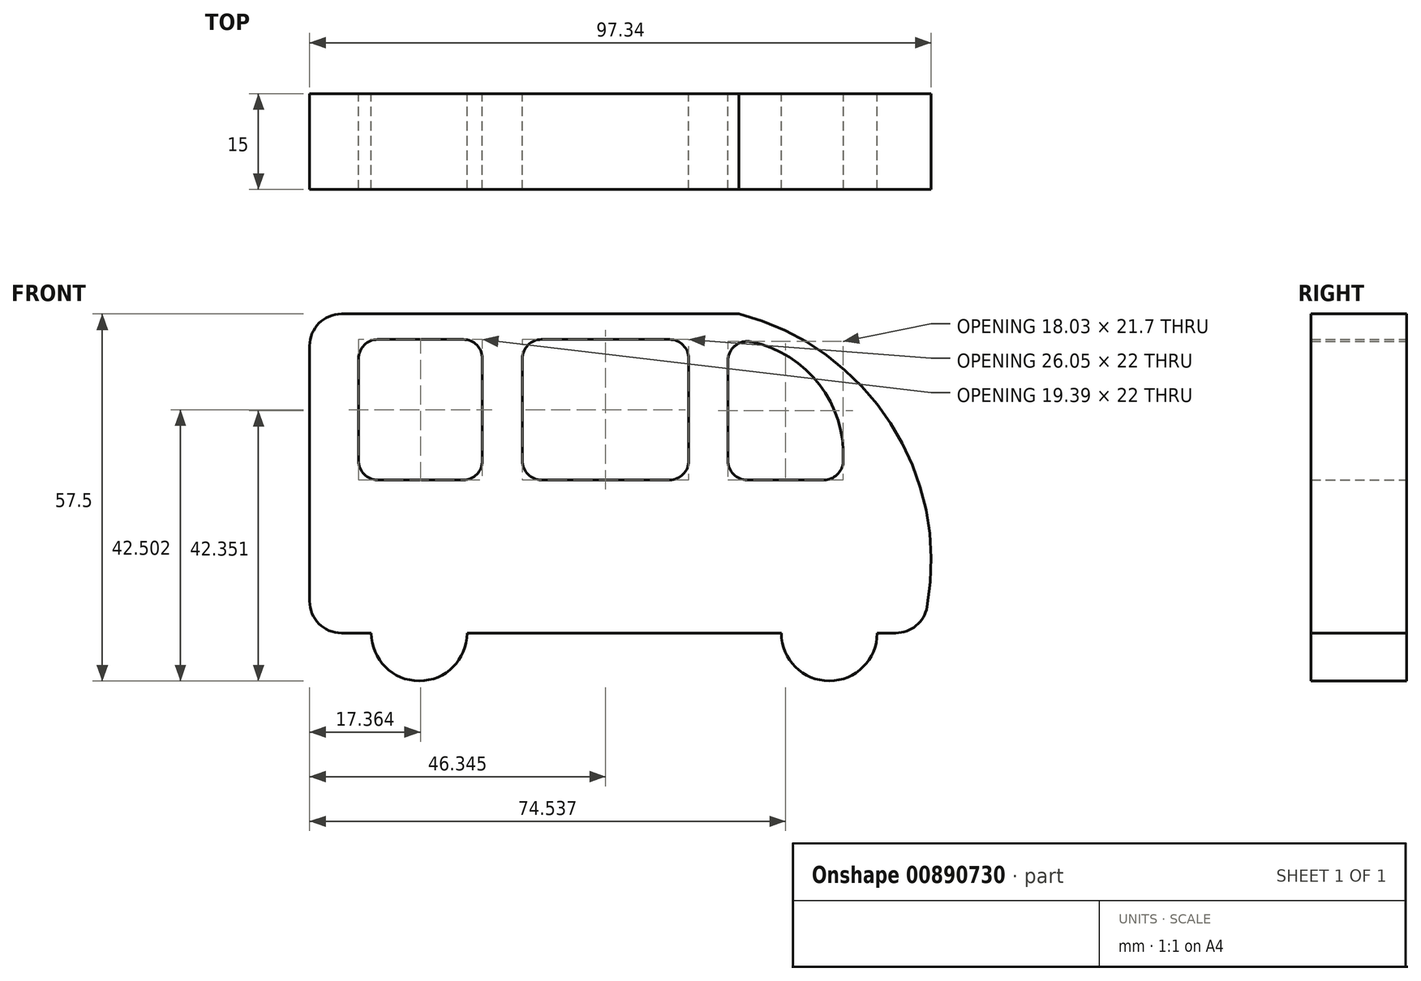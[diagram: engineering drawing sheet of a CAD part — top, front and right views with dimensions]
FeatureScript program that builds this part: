
annotation { "Feature Type Name" : "Feature", "Feature Type Description" : "" }
export const myFeature = defineFeature(function(context is Context, id is Id, definition is map)
    precondition{}
    {
        {
            var Q0;
            Q0=qCreatedBy(makeId("Front.planeOp"),FACE);
            var sketch = newSketch(context, id + "F0", { "sketchPlane" : qUnion([Q0])});
            skLineSegment(sketch, "E0.bottom", {"start": v(-16.93, 66.61) * mm, "end": v(45.28, 66.61) * mm});
            skLineSegment(sketch, "E0.top", {"start": v(-16.93, 16.61) * mm, "end": v(-12.27, 16.61) * mm});
            skLineSegment(sketch, "E0.left", {"start": v(-21.93, 61.61) * mm, "end": v(-21.93, 21.61) * mm});
            skArc(sketch, "E1", {"start": v(-12.27, 16.61) * mm, "mid": v(-4.77, 9.11) * mm, "end": v(2.73, 16.61) * mm});
            skArc(sketch, "E2", {"start": v(51.95, 16.61) * mm, "mid": v(59.45, 9.11) * mm, "end": v(66.95, 16.61) * mm});
            skArc(sketch, "E3", {"start": v(74.77, 20.72) * mm, "mid": v(69.06, 49.47) * mm, "end": v(45.28, 66.61) * mm});
            skPoint(sketch, "E4.visualSharp", {"position": v(-21.93, 66.61) * mm});
            skArc(sketch, "E4.filletArc", {"start": v(-16.93, 66.61) * mm, "mid": v(-20.47, 65.15) * mm, "end": v(-21.93, 61.61) * mm});
            skPoint(sketch, "E5.visualSharp", {"position": v(-21.93, 16.61) * mm});
            skArc(sketch, "E5.filletArc", {"start": v(-21.93, 21.61) * mm, "mid": v(-20.47, 18.08) * mm, "end": v(-16.93, 16.61) * mm});
            skPoint(sketch, "E6.visualSharp", {"position": v(73.8, 16.61) * mm});
            skArc(sketch, "E6.filletArc", {"start": v(69.85, 16.61) * mm, "mid": v(73.06, 17.77) * mm, "end": v(74.77, 20.72) * mm});
            skLineSegment(sketch, "E7.trimOffspring", {"start": v(2.73, 16.61) * mm, "end": v(51.95, 16.61) * mm});
            skLineSegment(sketch, "E8.trimOffspring", {"start": v(66.95, 16.61) * mm, "end": v(69.85, 16.61) * mm});
            skLineSegment(sketch, "E9", {"start": v(58.63, 40.61) * mm, "end": v(46.6, 40.61) * mm});
            skLineSegment(sketch, "E10", {"start": v(43.6, 43.61) * mm, "end": v(43.6, 59.31) * mm});
            skLineSegment(sketch, "E11.bottom", {"start": v(-11.26, 62.61) * mm, "end": v(2.13, 62.61) * mm});
            skLineSegment(sketch, "E11.top", {"start": v(-11.26, 40.61) * mm, "end": v(2.13, 40.61) * mm});
            skLineSegment(sketch, "E11.left", {"start": v(-14.26, 59.61) * mm, "end": v(-14.26, 43.61) * mm});
            skLineSegment(sketch, "E11.right", {"start": v(5.13, 59.61) * mm, "end": v(5.13, 43.61) * mm});
            skLineSegment(sketch, "E12.bottom", {"start": v(14.39, 62.61) * mm, "end": v(34.44, 62.61) * mm});
            skLineSegment(sketch, "E12.top", {"start": v(14.39, 40.61) * mm, "end": v(34.44, 40.61) * mm});
            skLineSegment(sketch, "E12.left", {"start": v(11.39, 59.61) * mm, "end": v(11.39, 43.61) * mm});
            skLineSegment(sketch, "E12.right", {"start": v(37.44, 59.61) * mm, "end": v(37.44, 43.61) * mm});
            skArc(sketch, "E13", {"start": v(61.62, 43.43) * mm, "mid": v(57.93, 55.54) * mm, "end": v(47.2, 62.25) * mm});
            skPoint(sketch, "E14.visualSharp", {"position": v(-14.26, 40.61) * mm});
            skArc(sketch, "E14.filletArc", {"start": v(-14.26, 43.61) * mm, "mid": v(-13.38, 41.5) * mm, "end": v(-11.26, 40.61) * mm});
            skPoint(sketch, "E15.visualSharp", {"position": v(-14.26, 62.61) * mm});
            skArc(sketch, "E15.filletArc", {"start": v(-11.26, 62.61) * mm, "mid": v(-13.38, 61.73) * mm, "end": v(-14.26, 59.61) * mm});
            skPoint(sketch, "E16.visualSharp", {"position": v(5.13, 62.61) * mm});
            skArc(sketch, "E16.filletArc", {"start": v(5.13, 59.61) * mm, "mid": v(4.25, 61.73) * mm, "end": v(2.13, 62.61) * mm});
            skPoint(sketch, "E17.visualSharp", {"position": v(5.13, 40.61) * mm});
            skArc(sketch, "E17.filletArc", {"start": v(2.13, 40.61) * mm, "mid": v(4.25, 41.5) * mm, "end": v(5.13, 43.61) * mm});
            skPoint(sketch, "E18.visualSharp", {"position": v(11.39, 40.61) * mm});
            skArc(sketch, "E18.filletArc", {"start": v(11.39, 43.61) * mm, "mid": v(12.27, 41.5) * mm, "end": v(14.39, 40.61) * mm});
            skPoint(sketch, "E19.visualSharp", {"position": v(11.39, 62.61) * mm});
            skArc(sketch, "E19.filletArc", {"start": v(14.39, 62.61) * mm, "mid": v(12.27, 61.73) * mm, "end": v(11.39, 59.61) * mm});
            skPoint(sketch, "E20.visualSharp", {"position": v(37.44, 62.61) * mm});
            skArc(sketch, "E20.filletArc", {"start": v(37.44, 59.61) * mm, "mid": v(36.56, 61.73) * mm, "end": v(34.44, 62.61) * mm});
            skPoint(sketch, "E21.visualSharp", {"position": v(37.44, 40.61) * mm});
            skArc(sketch, "E21.filletArc", {"start": v(34.44, 40.61) * mm, "mid": v(36.56, 41.5) * mm, "end": v(37.44, 43.61) * mm});
            skPoint(sketch, "E22.visualSharp", {"position": v(43.6, 40.61) * mm});
            skArc(sketch, "E22.filletArc", {"start": v(43.6, 43.61) * mm, "mid": v(44.47, 41.5) * mm, "end": v(46.6, 40.61) * mm});
            skPoint(sketch, "E23.visualSharp", {"position": v(43.6, 62.61) * mm});
            skArc(sketch, "E23.filletArc", {"start": v(47.2, 62.25) * mm, "mid": v(44.7, 61.63) * mm, "end": v(43.6, 59.31) * mm});
            skPoint(sketch, "E24.visualSharp", {"position": v(25.96, 40.61) * mm});
            skArc(sketch, "E24.filletArc", {"start": v(58.63, 40.61) * mm, "mid": v(60.68, 41.43) * mm, "end": v(61.62, 43.43) * mm});
            skSolve(sketch);
        }
        {
            var Q0;
            Q0=makeQuery(id+"F0.imprint","IMPRINT",FACE,{"disambiguationData":[TD([[makeQuery(id+"F0.imprint","IMPRINT",EDGE,{"derivedFrom":sQuery(id+"F0.wireOp",EDGE,"zIPLF4fH-aJVi-29oM-1MIk-gYxiGz5PzCoa.bottom")}),-1.0]])]});
            var Q1;
            Q1=makeQuery(id+"F0.imprint","IMPRINT",FACE,{"disambiguationData":[TD([[makeQuery(id+"F0.imprint","IMPRINT",EDGE,{"derivedFrom":sQuery(id+"F0.wireOp",EDGE,"E0.bottom")}),-1.0]])]});
            extrude(context, id + "F1", {"entities" : qUnion([Q0, Q1]), "depth" : 15 * mm, "offsetDistance" : 25 * mm});
        }
    });
